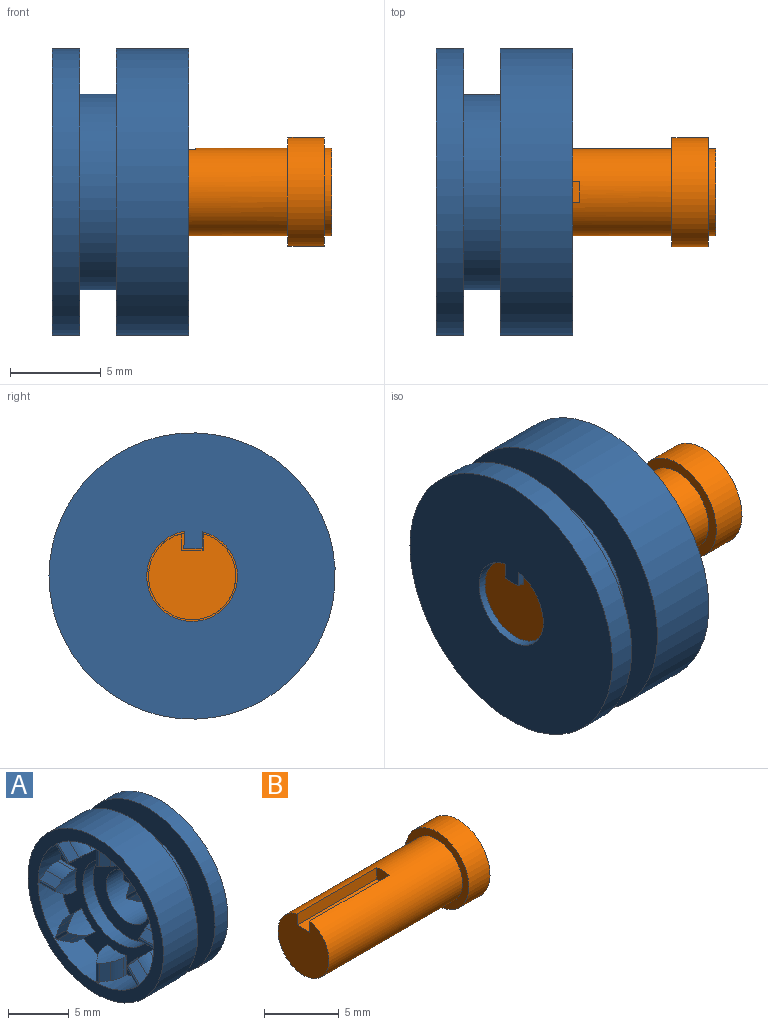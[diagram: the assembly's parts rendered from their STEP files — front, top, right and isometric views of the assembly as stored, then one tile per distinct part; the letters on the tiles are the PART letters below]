
ASSEMBLY  parts=2 mates=1
PART A: 79 faces, bbox 7.5x15.8x15.8 mm
  f0: cylinder r=2.5mm len=5mm, axis (-1,0,0), area 55.9mm2, adj f1,f2,f56,f77
  f1: plane 3.8x0.95mm, normal (0,-1,0), area 3.6mm2, adj f0,f3,f56,f77
  f2: plane 3.8x0.95mm, normal (0,1,0), area 3.6mm2, adj f0,f3,f56,f77
  f3: plane 3.8x1mm, normal (0,0,-1), area 3.8mm2, adj f1,f2,f56,f77
  f4: cylinder r=0.2mm len=1.85mm, axis (0,0,-1), area 0.7mm2, adj f44,f45,f52,f69
  f5: cylinder r=2mm len=1.94mm, axis (0,0,-1), area 2.4mm2, adj f28,f44,f45,f69
  f6: cylinder r=2mm len=1.94mm, axis (0,1,0), area 2.4mm2, adj f40,f44,f46,f75
  f7: cylinder r=0.2mm len=1.85mm, axis (0,1,0), area 0.7mm2, adj f44,f46,f66,f75
  f8: cylinder r=0.2mm len=1.54mm, axis (0,0.71,0.71), area 0.7mm2, adj f44,f47,f65,f74
  f9: cylinder r=2mm len=1.64mm, axis (0,0.71,0.71), area 2.4mm2, adj f38,f44,f47,f74
  f10: cylinder r=0.2mm len=1.85mm, axis (0,0,-1), area 0.7mm2, adj f44,f48,f64,f73
  f11: cylinder r=2mm len=1.94mm, axis (0,0,-1), area 2.4mm2, adj f30,f44,f48,f73
  f12: cylinder r=2mm len=1.64mm, axis (0,-0.71,0.71), area 2.4mm2, adj f35,f44,f49,f72
  f13: cylinder r=0.2mm len=1.54mm, axis (0,-0.71,0.71), area 0.7mm2, adj f44,f49,f63,f72
  f14: cylinder r=2mm len=1.94mm, axis (0,-1,0), area 2.4mm2, adj f33,f44,f50,f71
  f15: cylinder r=0.2mm len=1.85mm, axis (0,-1,0), area 0.7mm2, adj f44,f50,f62,f71
  f16: cylinder r=2mm len=1.64mm, axis (0,-0.71,-0.71), area 2.4mm2, adj f31,f44,f51,f70
  f17: cylinder r=0.2mm len=1.54mm, axis (0,-0.71,-0.71), area 0.7mm2, adj f44,f51,f61,f70
  f18: cylinder r=2mm len=1.94mm, axis (0,0,-1), area 2.4mm2, adj f29,f44,f52,f69
  f19: cylinder r=2mm len=1.64mm, axis (0,-0.71,-0.71), area 2.4mm2, adj f32,f44,f61,f70
  f20: cylinder r=2mm len=1.94mm, axis (0,-1,0), area 2.4mm2, adj f34,f44,f62,f71
  f21: cylinder r=2mm len=1.64mm, axis (0,-0.71,0.71), area 2.4mm2, adj f36,f44,f63,f72
  f22: cylinder r=2mm len=1.94mm, axis (0,0,1), area 2.4mm2, adj f37,f44,f64,f73
  f23: cylinder r=2mm len=1.64mm, axis (0,0.71,0.71), area 2.4mm2, adj f39,f44,f65,f74
  f24: cylinder r=2mm len=1.94mm, axis (0,1,0), area 2.4mm2, adj f41,f44,f66,f75
  f25: cylinder r=0.2mm len=1.54mm, axis (0,0.71,-0.71), area 0.7mm2, adj f44,f67,f68,f76
  f26: cylinder r=2mm len=1.64mm, axis (0,0.71,-0.71), area 2.4mm2, adj f42,f44,f67,f76
  f27: cylinder r=2mm len=1.64mm, axis (0,0.71,-0.71), area 2.4mm2, adj f43,f44,f68,f76
  f28: plane 1.89x0.35mm, normal (0,-1,0), area 0.7mm2, adj f5,f44,f53,f69
  f29: plane 1.89x0.35mm, normal (0,1,0), area 0.7mm2, adj f18,f44,f53,f69
  f30: plane 1.89x0.35mm, normal (0,-1,0), area 0.7mm2, adj f11,f44,f53,f73
  f31: plane 1.33x1.33mm, normal (0,0.71,-0.71), area 0.7mm2, adj f16,f44,f53,f70
  f32: plane 1.33x1.33mm, normal (0,-0.71,0.71), area 0.7mm2, adj f19,f44,f53,f70
  f33: plane 1.89x0.35mm, normal (0,0,-1), area 0.7mm2, adj f14,f44,f53,f71
  f34: plane 1.89x0.35mm, normal (0,0,1), area 0.7mm2, adj f20,f44,f53,f71
  f35: plane 1.33x1.33mm, normal (0,-0.71,-0.71), area 0.7mm2, adj f12,f44,f53,f72
  f36: plane 1.33x1.33mm, normal (0,0.71,0.71), area 0.7mm2, adj f21,f44,f53,f72
  f37: plane 1.89x0.35mm, normal (0,1,0), area 0.7mm2, adj f22,f44,f53,f73
  f38: plane 1.33x1.33mm, normal (0,-0.71,0.71), area 0.7mm2, adj f9,f44,f53,f74
  f39: plane 1.33x1.33mm, normal (0,0.71,-0.71), area 0.7mm2, adj f23,f44,f53,f74
  f40: plane 1.89x0.35mm, normal (0,0,1), area 0.7mm2, adj f6,f44,f53,f75
  f41: plane 1.89x0.35mm, normal (0,0,-1), area 0.7mm2, adj f24,f44,f53,f75
  f42: plane 1.33x1.33mm, normal (0,-0.71,-0.71), area 0.7mm2, adj f26,f44,f53,f76
  f43: plane 1.33x1.33mm, normal (0,0.71,0.71), area 0.7mm2, adj f27,f44,f53,f76
  f44: cylinder r=6.72mm len=13.45mm, axis (-1,0,0), area 75.6mm2, adj f4,f5,f6,f7,f8,f9,f10,f11
  f45: plane 1.9x0.75mm, normal (-0.59,-0.81,0), area 1.7mm2, adj f4,f5,f44,f69
  f46: plane 1.9x0.75mm, normal (-0.59,0,0.81), area 1.7mm2, adj f6,f7,f44,f75
  f47: plane 1.74x1.68mm, normal (-0.59,-0.57,0.57), area 1.7mm2, adj f8,f9,f44,f74
  f48: plane 1.9x0.75mm, normal (-0.59,-0.81,0), area 1.7mm2, adj f10,f11,f44,f73
  f49: plane 1.74x1.68mm, normal (-0.59,-0.57,-0.57), area 1.7mm2, adj f12,f13,f44,f72
  f50: plane 1.9x0.75mm, normal (-0.59,0,-0.81), area 1.7mm2, adj f14,f15,f44,f71
  f51: plane 1.74x1.68mm, normal (-0.59,0.57,-0.57), area 1.7mm2, adj f16,f17,f44,f70
  f52: plane 1.9x0.75mm, normal (-0.59,0.81,0), area 1.7mm2, adj f4,f18,f44,f69
  f53: plane 13.27x13.27mm, normal (-1,0,0), area 59.1mm2, adj f28,f29,f30,f31,f32,f33,f34,f35
  f54: cylinder r=7.88mm len=15.75mm, axis (-1,0,0), area 197.9mm2, adj f55,f60
  f55: plane 15.75x15.75mm, normal (-1,0,0), area 52.7mm2, adj f44,f54
  f56: plane 15.75x15.75mm, normal (1,0,0), area 176.2mm2, adj f0,f1,f2,f3,f57
  f57: cylinder r=7.88mm len=15.75mm, axis (-1,0,0), area 74.2mm2, adj f56,f58
  f58: plane 15.75x15.75mm, normal (-1,0,0), area 104.1mm2, adj f57,f59
  f59: cylinder r=5.38mm len=10.75mm, axis (-1,0,0), area 67.5mm2, adj f58,f60
  f60: plane 15.75x15.75mm, normal (1,0,0), area 104.1mm2, adj f54,f59
  f61: plane 1.74x1.68mm, normal (-0.59,-0.57,0.57), area 1.7mm2, adj f17,f19,f44,f70
  f62: plane 1.9x0.75mm, normal (-0.59,0,0.81), area 1.7mm2, adj f15,f20,f44,f71
  f63: plane 1.74x1.68mm, normal (-0.59,0.57,0.57), area 1.7mm2, adj f13,f21,f44,f72
  f64: plane 1.9x0.75mm, normal (-0.59,0.81,0), area 1.7mm2, adj f10,f22,f44,f73
  f65: plane 1.74x1.68mm, normal (-0.59,0.57,-0.57), area 1.7mm2, adj f8,f23,f44,f74
  f66: plane 1.9x0.75mm, normal (-0.59,0,-0.81), area 1.7mm2, adj f7,f24,f44,f75
  f67: plane 1.74x1.68mm, normal (-0.59,-0.57,-0.57), area 1.7mm2, adj f25,f26,f44,f76
  f68: plane 1.74x1.68mm, normal (-0.59,0.57,0.57), area 1.7mm2, adj f25,f27,f44,f76
  f69: cylinder r=4.88mm len=2.36mm, axis (1,0,0), area 3.8mm2, adj f4,f5,f18,f28,f29,f45,f52,f53
  f70: cylinder r=4.88mm len=2.36mm, axis (1,0,0), area 3.8mm2, adj f16,f17,f19,f31,f32,f51,f53,f61
  f71: cylinder r=4.88mm len=2.36mm, axis (1,0,0), area 3.8mm2, adj f14,f15,f20,f33,f34,f50,f53,f62
  f72: cylinder r=4.88mm len=2.36mm, axis (1,0,0), area 3.8mm2, adj f12,f13,f21,f35,f36,f49,f53,f63
  f73: cylinder r=4.88mm len=2.36mm, axis (1,0,0), area 3.8mm2, adj f10,f11,f22,f30,f37,f48,f53,f64
  f74: cylinder r=4.88mm len=2.36mm, axis (1,0,0), area 3.8mm2, adj f8,f9,f23,f38,f39,f47,f53,f65
  f75: cylinder r=4.88mm len=2.36mm, axis (1,0,0), area 3.8mm2, adj f6,f7,f24,f40,f41,f46,f53,f66
  f76: cylinder r=4.88mm len=2.36mm, axis (1,0,0), area 3.8mm2, adj f25,f26,f27,f42,f43,f53,f67,f68
  f77: plane 8x8mm, normal (-1,0,0), area 31.6mm2, adj f0,f1,f2,f3,f78
  f78: cylinder r=4mm len=8mm, axis (-1,0,0), area 30.2mm2, adj f53,f77
PART B: 11 faces, bbox 15x6x6 mm
  f0: cylinder r=2.4mm len=12.6mm, axis (-1,0,0), area 180.9mm2, adj f1,f2,f3,f4,f7
  f1: plane 4.8x4.72mm, normal (-1,0,0), area 16.9mm2, adj f0,f3,f4,f5
  f2: plane 1.2x1mm, normal (-1,0,0), area 1.2mm2, adj f0,f3,f4,f5
  f3: plane 7.5x0.92mm, normal (0,-1,0), area 6.9mm2, adj f0,f1,f2,f5
  f4: plane 7.5x0.92mm, normal (0,1,0), area 6.9mm2, adj f0,f1,f2,f5
  f5: plane 7.5x1.2mm, normal (0,0,1), area 9mm2, adj f1,f2,f3,f4
  f6: cylinder r=3mm len=6mm, axis (-1,0,0), area 37.7mm2, adj f7,f8
  f7: plane 6x6mm, normal (-1,0,0), area 10.2mm2, adj f0,f6
  f8: plane 6x6mm, normal (1,0,0), area 10.2mm2, adj f6,f10
  f9: plane 4.8x4.8mm, normal (1,0,0), area 18.1mm2, adj f10
  f10: cylinder r=2.4mm len=4.8mm, axis (-1,0,0), area 6mm2, adj f8,f9
PLACE A rot(axis=(0,-0.02,1),180deg) t=(3.78,10.75,10.75)mm
PLACE B t=(-3.36,10.75,10.75)mm fixed
MATE cylindrical A.f0 <-> B.f0  axis (1,0,0) through (0.08,10.75,10.75)mm
